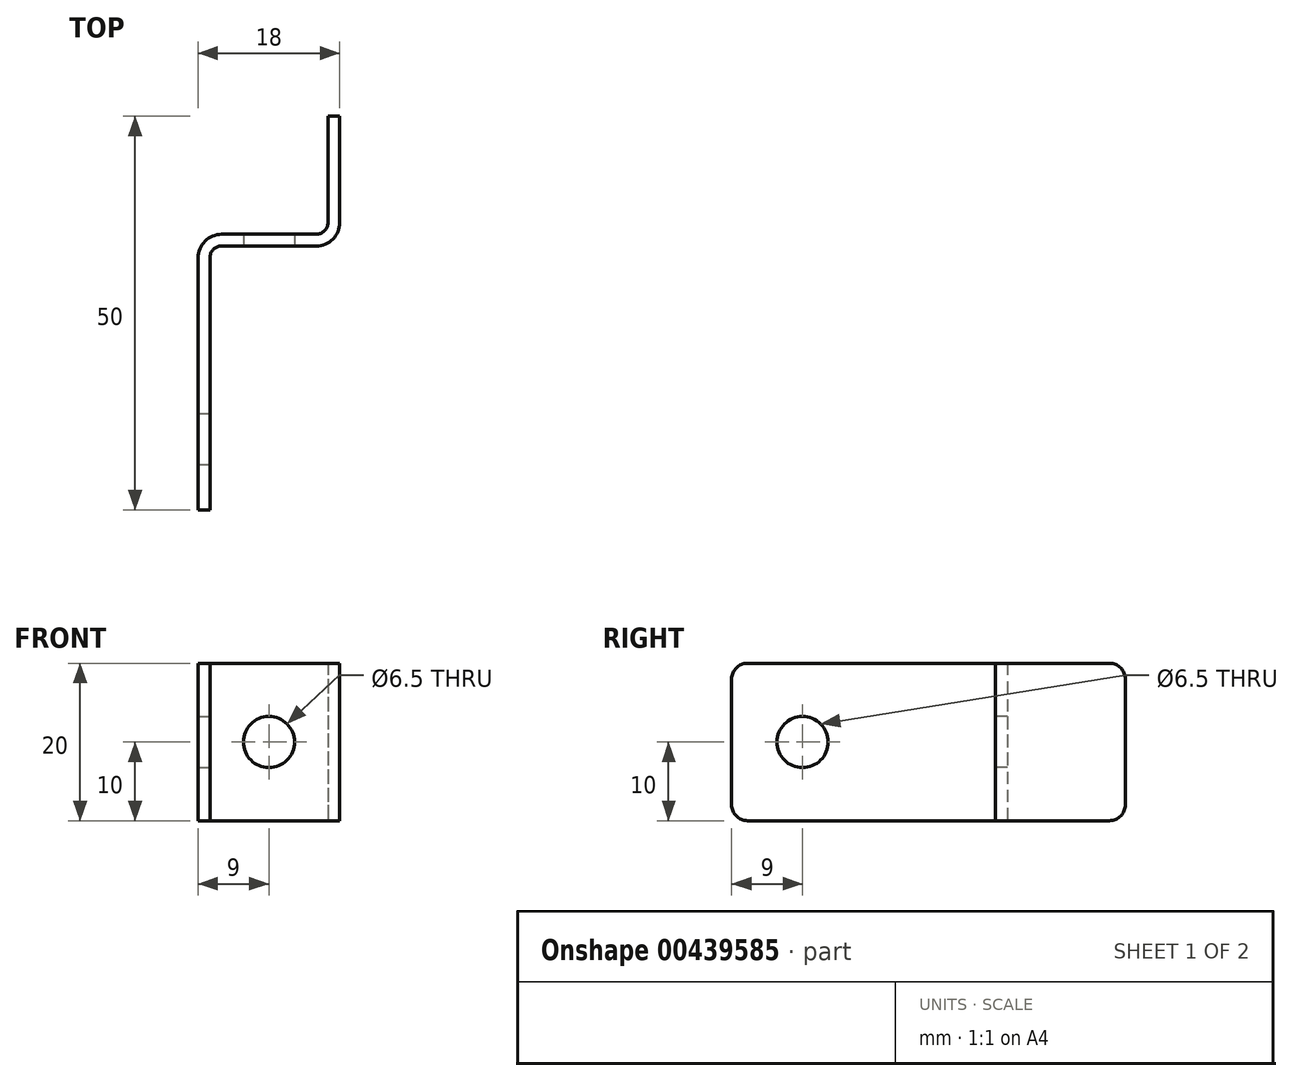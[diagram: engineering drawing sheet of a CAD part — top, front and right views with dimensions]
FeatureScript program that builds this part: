
annotation { "Feature Type Name" : "Feature", "Feature Type Description" : "" }
export const myFeature = defineFeature(function(context is Context, id is Id, definition is map)
    precondition{}
    {
        {
            var Q0;
            Q0=qCreatedBy(makeId("Top.planeOp"),FACE);
            var sketch = newSketch(context, id + "F0", { "sketchPlane" : qUnion([Q0])});
            skLineSegment(sketch, "E0", {"start": v(0, 0) * mm, "end": v(0, 32) * mm});
            skLineSegment(sketch, "E1", {"start": v(3, 35) * mm, "end": v(15, 35) * mm});
            skLineSegment(sketch, "E2", {"start": v(16.5, 36.5) * mm, "end": v(16.5, 50) * mm});
            skLineSegment(sketch, "E3", {"start": v(16.5, 50) * mm, "end": v(18, 50) * mm});
            skLineSegment(sketch, "E4", {"start": v(18, 50) * mm, "end": v(18, 36.5) * mm});
            skLineSegment(sketch, "E5", {"start": v(15, 33.5) * mm, "end": v(3, 33.5) * mm});
            skLineSegment(sketch, "E6", {"start": v(1.5, 32) * mm, "end": v(1.5, 0) * mm});
            skLineSegment(sketch, "E7", {"start": v(1.5, 0) * mm, "end": v(0, 0) * mm});
            skPoint(sketch, "E8.visualSharp", {"position": v(1.5, 33.5) * mm});
            skArc(sketch, "E8.filletArc", {"start": v(3, 33.5) * mm, "mid": v(1.94, 33.06) * mm, "end": v(1.5, 32) * mm});
            skPoint(sketch, "E9.visualSharp", {"position": v(16.5, 35) * mm});
            skArc(sketch, "E9.filletArc", {"start": v(15, 35) * mm, "mid": v(16.06, 35.44) * mm, "end": v(16.5, 36.5) * mm});
            skPoint(sketch, "E10.visualSharp", {"position": v(18, 33.5) * mm});
            skArc(sketch, "E10.filletArc", {"start": v(15, 33.5) * mm, "mid": v(17.12, 34.38) * mm, "end": v(18, 36.5) * mm});
            skPoint(sketch, "E11.visualSharp", {"position": v(0, 35) * mm});
            skArc(sketch, "E11.filletArc", {"start": v(3, 35) * mm, "mid": v(0.88, 34.12) * mm, "end": v(0, 32) * mm});
            skSolve(sketch);
        }
        {
            var Q0;
            Q0=makeQuery(id+"F0.imprint","IMPRINT",FACE,{"disambiguationData":[TD([[makeQuery(id+"F0.imprint","IMPRINT",EDGE,{"derivedFrom":sQuery(id+"F0.wireOp",EDGE,"E0")}),-1.0]])]});
            extrude(context, id + "F1", {"entities" : qUnion([Q0]), "depth" : 20 * mm});
        }
        {
            var Q0;
            Q0=makeQuery(id+"F1.opExtrude","CAP_EDGE",EDGE,{"disambiguationData":[OSD([sQuery(id+"F0.wireOp",EDGE,"E7")])],"isStart":false});
            var Q1;
            Q1=makeQuery(id+"F1.opExtrude","CAP_EDGE",EDGE,{"disambiguationData":[OSD([sQuery(id+"F0.wireOp",EDGE,"E7")])],"isStart":true});
            var Q2;
            Q2=makeQuery(id+"F1.opExtrude","CAP_EDGE",EDGE,{"disambiguationData":[OSD([sQuery(id+"F0.wireOp",EDGE,"E3")])],"isStart":false});
            var Q3;
            Q3=makeQuery(id+"F1.opExtrude","CAP_EDGE",EDGE,{"disambiguationData":[OSD([sQuery(id+"F0.wireOp",EDGE,"E3")])],"isStart":true});
            fillet(context, id + "F2", {"entities" : qUnion([Q0, Q1, Q2, Q3]), "radius" : 2 * mm, "tangentPropagation" : true, "allowEdgeOverflow" : false});
        }
        {
            var Q0;
            Q0=makeQuery(id+"F1.opExtrude","SWEPT_FACE",FACE,{"disambiguationData":[OSD([sQuery(id+"F0.wireOp",EDGE,"E4")])]});
            var sketch = newSketch(context, id + "F3", { "sketchPlane" : qUnion([Q0])});
            skCircle(sketch, "E12", {"center": v(9, 10) * mm, "radius": 3.25 * mm});
            skPoint(sketch, "E13", {"position": v(50, 10) * mm});
            skSolve(sketch);
        }
        {
            var Q0;
            Q0=makeQuery(id+"F3.imprint","IMPRINT",FACE,{"disambiguationData":[TD([[makeQuery(id+"F3.imprint","IMPRINT",EDGE,{"derivedFrom":sQuery(id+"F3.wireOp",EDGE,"E12")}),1.0]])]});
            extrude(context, id + "F4", {"entities" : qUnion([Q0]), "operationType" : NewBodyOperationType.REMOVE, "oppositeDirection" : true, "depth" : 50 * mm});
        }
        {
            var Q0;
            Q0=makeQuery(id+"F1.opExtrude","SWEPT_FACE",FACE,{"disambiguationData":[OSD([sQuery(id+"F0.wireOp",EDGE,"E5")])]});
            var sketch = newSketch(context, id + "F5", { "sketchPlane" : qUnion([Q0])});
            skCircle(sketch, "E14", {"center": v(9, 10) * mm, "radius": 3.25 * mm});
            skSolve(sketch);
        }
        {
            var Q0;
            Q0=makeQuery(id+"F5.imprint","IMPRINT",FACE,{"disambiguationData":[TD([[makeQuery(id+"F5.imprint","IMPRINT",EDGE,{"derivedFrom":sQuery(id+"F5.wireOp",EDGE,"E14")}),1.0]])]});
            extrude(context, id + "F6", {"entities" : qUnion([Q0]), "operationType" : NewBodyOperationType.REMOVE, "oppositeDirection" : true, "depth" : 25 * mm});
        }
    });
